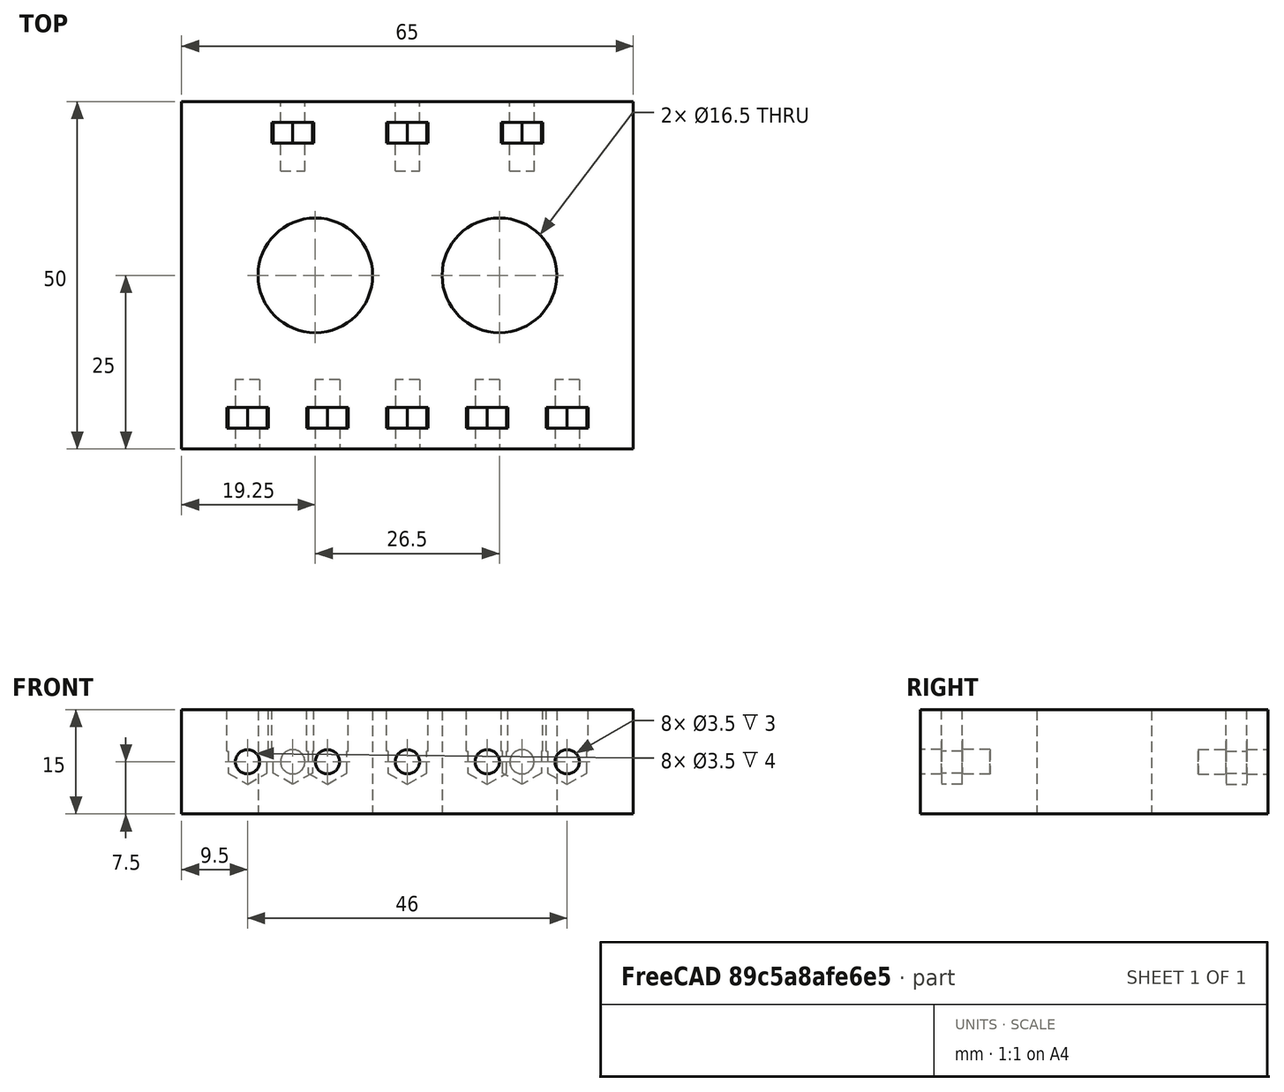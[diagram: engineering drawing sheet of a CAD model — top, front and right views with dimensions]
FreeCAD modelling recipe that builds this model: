
FCSTD DOCUMENT  (FreeCAD 0.19R14555 (Git shallow))
Label: Soporte delantero
License: All rights reserved
LicenseURL: http://en.wikipedia.org/wiki/All_rights_reserved
objects: Part::MultiFuse×11, Part::Cylinder×10, Part::Box×9, Part::Prism×8, Part::Cut×3
note: 41 computed .brp shape members not serialized (recipe doc carries the construction recipe); baked Part::Feature solids carry a one-line shape summary decoded from their .brp

FEATURE [Part::Cylinder] Cylinder  label="Cilindro"
  Angle = 360
  AttacherType = Attacher::AttachEngine3D
  Height = 20
  Placement = pos=(10,10,0) rot=(0,0,1;0rad)
  Radius = 8.25
FEATURE [Part::Cylinder] Cylinder001  label="Cilindro001"
  Angle = 360
  AttacherType = Attacher::AttachEngine3D
  Height = 20
  Placement = pos=(10,36.5,0) rot=(0,0,1;0rad)
  Radius = 8.25
FEATURE [Part::MultiFuse] Fusion
  Placement = pos=(55.75,17,15) rot=(0.57735,-0.57735,0.57735;2.0944rad)
  Shapes = -> [Cylinder,Cylinder001]
FEATURE [Part::Box] Box  label="Cubo"
  AttacherType = Attacher::AttachEngine3D
  Height = 50
  Length = 65
  Width = 15
FEATURE [Part::Box] Box009  label="Cubo009"
  AttacherType = Attacher::AttachEngine3D
  Height = 3
  Length = 6
  Placement = pos=(31,9,3) rot=(0,0,1;0rad)
  Width = 20
FEATURE [Part::Cylinder] Cylinder009  label="Cilindro009"
  Angle = 360
  AttacherType = Attacher::AttachEngine3D
  Height = 20
  Placement = pos=(34,7.5,-1) rot=(0,0,1;0rad)
  Radius = 1.75
FEATURE [Part::Prism] Prism007  label="Prisma007"
  AttacherType = Attacher::AttachEngine3D
  Circumradius = 3.25
  FirstAngle = 0
  Height = 3
  Placement = pos=(34,7.5,3) rot=(0,0,1;1.5708rad)
  Polygon = 6
  SecondAngle = 0
FEATURE [Part::MultiFuse] Fusion009
  Placement = pos=(-21,0,41) rot=(1,0,0;0rad)
  Shapes = -> [Box009,Prism007,Cylinder009]
FEATURE [Part::Cut] Cut
  Base = -> Box
  Tool = -> Fusion
FEATURE [Part::Box] Box010  label="Cubo010"
  AttacherType = Attacher::AttachEngine3D
  Height = 3
  Length = 6
  Placement = pos=(31,9,3) rot=(0,0,1;0rad)
  Width = 20
FEATURE [Part::Cylinder] Cylinder010  label="Cilindro010"
  Angle = 360
  AttacherType = Attacher::AttachEngine3D
  Height = 20
  Placement = pos=(34,7.5,-1) rot=(0,0,1;0rad)
  Radius = 1.75
FEATURE [Part::Prism] Prism008  label="Prisma008"
  AttacherType = Attacher::AttachEngine3D
  Circumradius = 3.25
  FirstAngle = 0
  Height = 3
  Placement = pos=(34,7.5,3) rot=(0,0,1;1.5708rad)
  Polygon = 6
  SecondAngle = 0
FEATURE [Part::MultiFuse] Fusion010
  Placement = pos=(-9.5,0,41) rot=(1,0,0;0rad)
  Shapes = -> [Box010,Prism008,Cylinder010]
FEATURE [Part::Box] Box011  label="Cubo011"
  AttacherType = Attacher::AttachEngine3D
  Height = 3
  Length = 6
  Placement = pos=(31,9,3) rot=(0,0,1;0rad)
  Width = 20
FEATURE [Part::Prism] Prism009  label="Prisma009"
  AttacherType = Attacher::AttachEngine3D
  Circumradius = 3.25
  FirstAngle = 0
  Height = 3
  Placement = pos=(34,7.5,3) rot=(0,0,1;1.5708rad)
  Polygon = 6
  SecondAngle = 0
FEATURE [Part::Cylinder] Cylinder011  label="Cilindro011"
  Angle = 360
  AttacherType = Attacher::AttachEngine3D
  Height = 20
  Placement = pos=(34,7.5,-1) rot=(0,0,1;0rad)
  Radius = 1.75
FEATURE [Part::MultiFuse] Fusion011
  Placement = pos=(2,0,41) rot=(1,0,0;0rad)
  Shapes = -> [Box011,Prism009,Cylinder011]
FEATURE [Part::Cylinder] Cylinder012  label="Cilindro012"
  Angle = 360
  AttacherType = Attacher::AttachEngine3D
  Height = 20
  Placement = pos=(34,7.5,-1) rot=(0,0,1;0rad)
  Radius = 1.75
FEATURE [Part::Prism] Prism010  label="Prisma010"
  AttacherType = Attacher::AttachEngine3D
  Circumradius = 3.25
  FirstAngle = 0
  Height = 3
  Placement = pos=(34,7.5,3) rot=(0,0,1;1.5708rad)
  Polygon = 6
  SecondAngle = 0
FEATURE [Part::Box] Box012  label="Cubo012"
  AttacherType = Attacher::AttachEngine3D
  Height = 3
  Length = 6
  Placement = pos=(31,9,3) rot=(0,0,1;0rad)
  Width = 20
FEATURE [Part::MultiFuse] Fusion012
  Placement = pos=(13.5,0,41) rot=(1,0,0;0rad)
  Shapes = -> [Box012,Prism010,Cylinder012]
FEATURE [Part::Box] Box013  label="Cubo013"
  AttacherType = Attacher::AttachEngine3D
  Height = 3
  Length = 6
  Placement = pos=(31,9,3) rot=(0,0,1;0rad)
  Width = 20
FEATURE [Part::Cylinder] Cylinder013  label="Cilindro013"
  Angle = 360
  AttacherType = Attacher::AttachEngine3D
  Height = 20
  Placement = pos=(34,7.5,-1) rot=(0,0,1;0rad)
  Radius = 1.75
FEATURE [Part::Prism] Prism011  label="Prisma011"
  AttacherType = Attacher::AttachEngine3D
  Circumradius = 3.25
  FirstAngle = 0
  Height = 3
  Placement = pos=(34,7.5,3) rot=(0,0,1;1.5708rad)
  Polygon = 6
  SecondAngle = 0
FEATURE [Part::MultiFuse] Fusion013
  Placement = pos=(25,0,41) rot=(1,0,0;0rad)
  Shapes = -> [Box013,Prism011,Cylinder013]
FEATURE [Part::MultiFuse] Fusion014
  Placement = pos=(-3.5,0,0) rot=(0,0,1;0rad)
  Shapes = -> [Fusion013,Fusion010,Fusion011,Fusion012,Fusion009]
FEATURE [Part::Cut] Cut001
  Base = -> Cut
  Tool = -> Fusion014
FEATURE [Part::Prism] Prism012  label="Prisma012"
  AttacherType = Attacher::AttachEngine3D
  Circumradius = 3.25
  FirstAngle = 0
  Height = 3
  Placement = pos=(34,7.5,3) rot=(0,0,1;1.5708rad)
  Polygon = 6
  SecondAngle = 0
FEATURE [Part::Cylinder] Cylinder014  label="Cilindro014"
  Angle = 360
  AttacherType = Attacher::AttachEngine3D
  Height = 20
  Placement = pos=(34,7.5,-1) rot=(0,0,1;0rad)
  Radius = 1.75
FEATURE [Part::Box] Box014  label="Cubo014"
  AttacherType = Attacher::AttachEngine3D
  Height = 3
  Length = 6
  Placement = pos=(31,9,3) rot=(0,0,1;0rad)
  Width = 20
FEATURE [Part::MultiFuse] Fusion015
  Placement = pos=(44,0,9) rot=(0,1,0;3.14159rad)
  Shapes = -> [Box014,Prism012,Cylinder014]
FEATURE [Part::Box] Box015  label="Cubo015"
  AttacherType = Attacher::AttachEngine3D
  Height = 3
  Length = 6
  Placement = pos=(31,9,3) rot=(0,0,1;0rad)
  Width = 20
FEATURE [Part::Cylinder] Cylinder015  label="Cilindro015"
  Angle = 360
  AttacherType = Attacher::AttachEngine3D
  Height = 20
  Placement = pos=(34,7.5,-1) rot=(0,0,1;0rad)
  Radius = 1.75
FEATURE [Part::Prism] Prism013  label="Prisma013"
  AttacherType = Attacher::AttachEngine3D
  Circumradius = 3.25
  FirstAngle = 0
  Height = 3
  Placement = pos=(34,7.5,3) rot=(0,0,1;1.5708rad)
  Polygon = 6
  SecondAngle = 0
FEATURE [Part::MultiFuse] Fusion016
  Placement = pos=(60.5,0,9) rot=(0,1,0;3.14159rad)
  Shapes = -> [Box015,Prism013,Cylinder015]
FEATURE [Part::Prism] Prism014  label="Prisma014"
  AttacherType = Attacher::AttachEngine3D
  Circumradius = 3.25
  FirstAngle = 0
  Height = 3
  Placement = pos=(34,7.5,3) rot=(0,0,1;1.5708rad)
  Polygon = 6
  SecondAngle = 0
FEATURE [Part::Box] Box016  label="Cubo016"
  AttacherType = Attacher::AttachEngine3D
  Height = 3
  Length = 6
  Placement = pos=(31,9,3) rot=(0,0,1;0rad)
  Width = 20
FEATURE [Part::Cylinder] Cylinder016  label="Cilindro016"
  Angle = 360
  AttacherType = Attacher::AttachEngine3D
  Height = 20
  Placement = pos=(34,7.5,-1) rot=(0,0,1;0rad)
  Radius = 1.75
FEATURE [Part::MultiFuse] Fusion017
  Placement = pos=(77,0,9) rot=(0,1,0;3.14159rad)
  Shapes = -> [Box016,Prism014,Cylinder016]
FEATURE [Part::MultiFuse] Fusion018
  Placement = pos=(6,0,0) rot=(0,0,1;0rad)
  Shapes = -> [Fusion017,Fusion015,Fusion016]
FEATURE [Part::Cut] Cut002
  Base = -> Cut001
  Placement = pos=(0,0,0) rot=(1,0,0;1.5708rad)
  Tool = -> Fusion018
